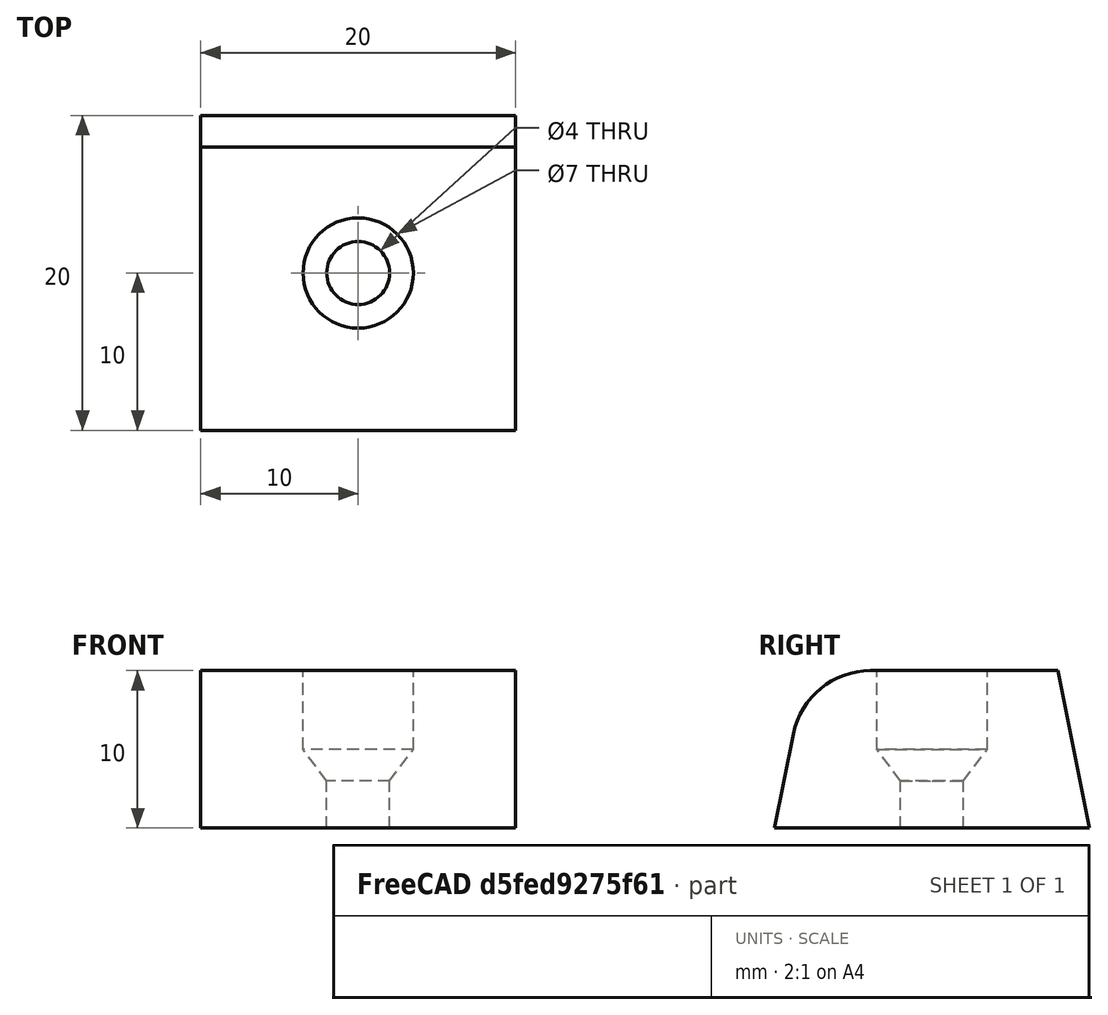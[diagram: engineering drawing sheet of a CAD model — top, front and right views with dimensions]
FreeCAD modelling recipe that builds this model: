
FCSTD DOCUMENT  (FreeCAD 0.16R6703 (Git))
Label: Anclaje Placa Inferior
License: All rights reserved
LicenseURL: http://en.wikipedia.org/wiki/All_rights_reserved
objects: Part::Cylinder×2, Part::Wedge×1, Part::Cone×1, Part::MultiFuse×1, Part::Fillet×1, Part::Cut×1
note: 7 computed .brp shape members not serialized (recipe doc carries the construction recipe); baked Part::Feature solids carry a one-line shape summary decoded from their .brp

FEATURE [Part::Wedge] Wedge
  Placement = pos=(0,0,0) rot=(1,0,0;1.5708rad)
  X2max = 20
  X2min = 0
  Xmax = 20
  Xmin = 0
  Ymax = 10
  Ymin = 0
  Z2max = 18
  Z2min = 2
  Zmax = 20
  Zmin = 0
FEATURE [Part::Cylinder] Cylinder
  Angle = 360
  Height = 10
  Placement = pos=(15,-5,0) rot=(0,0,1;0rad)
  Radius = 2
FEATURE [Part::Cylinder] Cylinder001
  Angle = 360
  Height = 10
  Placement = pos=(15,-5,5) rot=(0,0,1;0rad)
  Radius = 3.5
FEATURE [Part::Cone] Cone
  Angle = 360
  Height = 2
  Placement = pos=(15,-5,3) rot=(0,0,1;0rad)
  Radius1 = 2
  Radius2 = 3.5
FEATURE [Part::MultiFuse] Fusion
  Placement = pos=(-5,-5,0) rot=(0,0,1;0rad)
  Shapes = -> [Cylinder,Cylinder001,Cone]
FEATURE [Part::Fillet] Fillet
  Base = -> Wedge
  Edges = 1 edges r=5: [Edge12]
FEATURE [Part::Cut] Cut
  Base = -> Fillet
  Tool = -> Fusion
